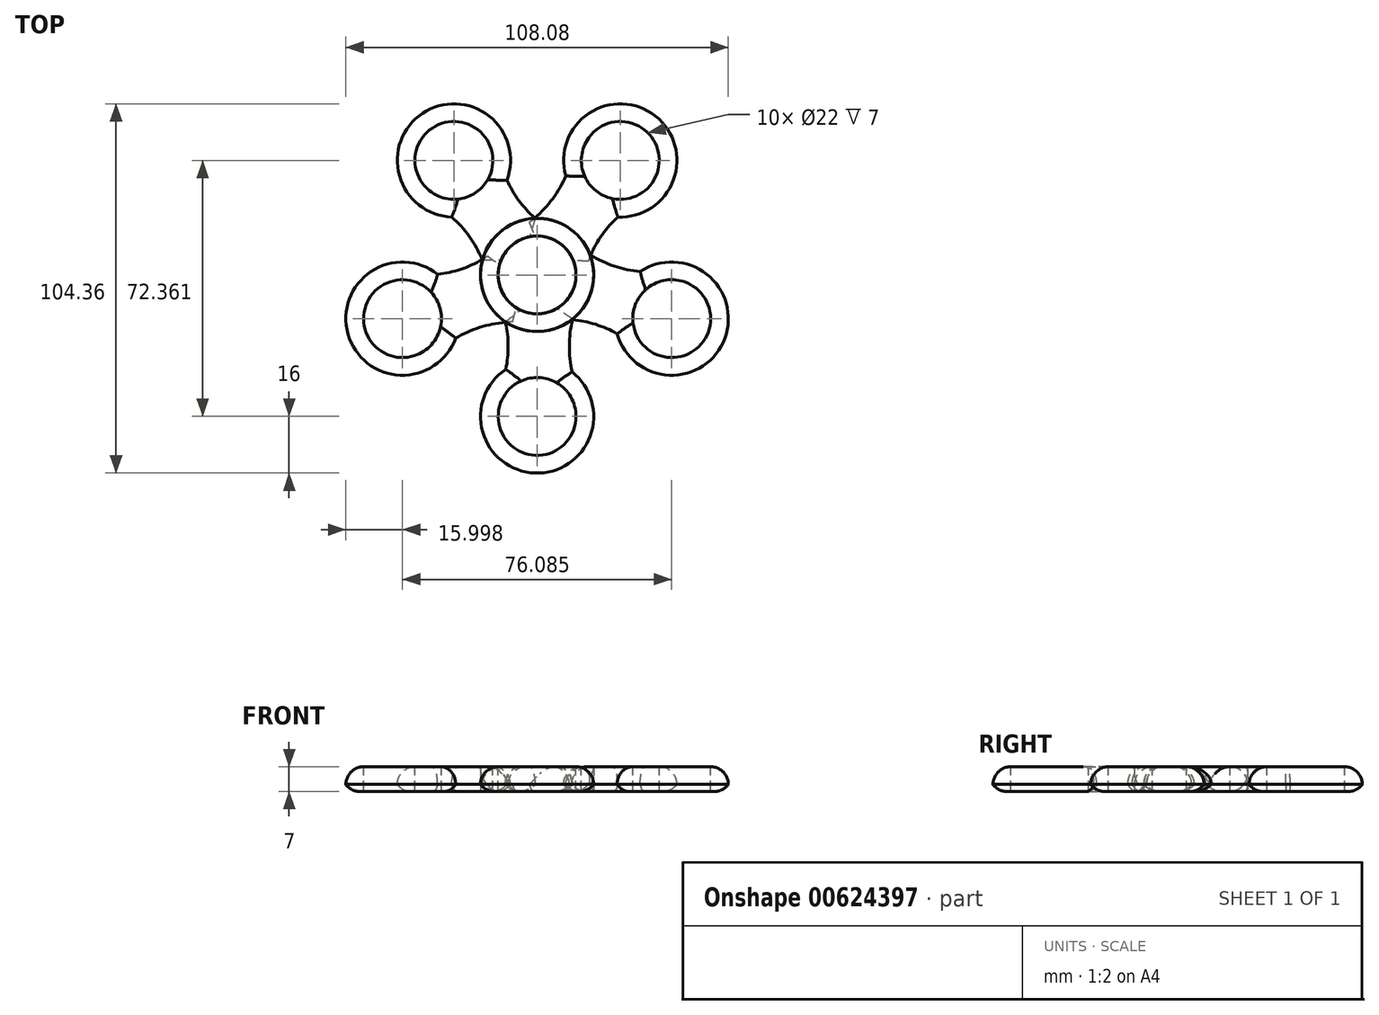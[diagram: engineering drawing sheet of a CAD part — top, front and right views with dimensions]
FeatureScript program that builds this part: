
annotation { "Feature Type Name" : "Feature", "Feature Type Description" : "" }
export const myFeature = defineFeature(function(context is Context, id is Id, definition is map)
    precondition{}
    {
        {
            var Q0;
            Q0=qCreatedBy(makeId("Top.planeOp"),FACE);
            var sketch = newSketch(context, id + "F0", { "sketchPlane" : qUnion([Q0])});
            skCircle(sketch, "E0", {"center": v(0, 0) * mm, "radius": 16 * mm});
            skCircle(sketch, "E1", {"center": v(0, -40) * mm, "radius": 16 * mm});
            skArc(sketch, "E2", {"start": v(-16, -40.55) * mm, "mid": v(-8.17, -20.27) * mm, "end": v(-16, 0) * mm});
            skArc(sketch, "E3", {"start": v(16, 0) * mm, "mid": v(9.11, -20.27) * mm, "end": v(16, -40.55) * mm});
            skSolve(sketch);
        }
        {
            var Q0;
            Q0 = qSketchRegion(id + "F0", true);
            extrude(context, id + "F1", {"entities" : qUnion([Q0]), "depth" : 7 * mm, "offsetDistance" : 25 * mm});
        }
        {
            var Q0;
            Q0=makeQuery(id+"F1.opExtrude","CAP_FACE",FACE,{"disambiguationData":[OSD([sQuery(id+"F0.wireOp",EDGE,"E0"),sQuery(id+"F0.wireOp",EDGE,"E1"),sQuery(id+"F0.wireOp",EDGE,"Ue3lBEtB-XySh-TUo9-pEQx-awfWVajxnvRm"),sQuery(id+"F0.wireOp",EDGE,"Egq79wn7-ryfj-ZDxT-aGIX-HA1hZmSv7uEE")])],"isStart":false});
            var sketch = newSketch(context, id + "F2", { "sketchPlane" : qUnion([Q0])});
            skCircle(sketch, "E4", {"center": v(0, 0) * mm, "radius": 11 * mm});
            skCircle(sketch, "E5", {"center": v(0, -40) * mm, "radius": 11 * mm});
            skSolve(sketch);
        }
        {
            var Q0;
            Q0 = qSketchRegion(id + "F2", true);
            extrude(context, id + "F3", {"entities" : qUnion([Q0]), "operationType" : NewBodyOperationType.REMOVE, "endBound" : BoundingType.THROUGH_ALL, "oppositeDirection" : true, "depth" : 25 * mm, "offsetDistance" : 25 * mm});
        }
        {
            var Q0;
            Q0=qCreatedBy(makeId("Front.planeOp"),FACE);
            var sketch = newSketch(context, id + "F4", { "sketchPlane" : qUnion([Q0])});
            skLineSegment(sketch, "E6", {"start": v(0, 0) * mm, "end": v(0, 23.09) * mm});
            skSolve(sketch);
        }
        {
            var Q0;
            Q0=makeQuery(id+"F1.opExtrude","SWEPT_BODY",BODY,{"disambiguationData":[OSD([sQuery(id+"F0.wireOp",EDGE,"E0"),sQuery(id+"F0.wireOp",EDGE,"E1"),sQuery(id+"F0.wireOp",EDGE,"Ue3lBEtB-XySh-TUo9-pEQx-awfWVajxnvRm"),sQuery(id+"F0.wireOp",EDGE,"Egq79wn7-ryfj-ZDxT-aGIX-HA1hZmSv7uEE")])]});
            var Q1;
            Q1=sQuery(id+"F4.wireOp",EDGE,"E6");
            circularPattern(context, id + "F5", {"entities" : qUnion([Q0]), "axis" : qUnion([Q1]), "angle" : 360 * degree, "instanceCount" : 5, "equalSpace" : true});
        }
        {
            var Q0;
            Q0=makeQuery(id+"F5.opPattern","COPY",EDGE,{"derivedFrom":makeQuery(id+"F1.opExtrude","CAP_EDGE",EDGE,{"disambiguationData":[OSD([sQuery(id+"F0.wireOp",EDGE,"E1")])],"isStart":false}),"instanceName":"4"});
            var Q1;
            Q1=makeQuery(id+"F5.opPattern","COPY",EDGE,{"derivedFrom":makeQuery(id+"F1.opExtrude","CAP_EDGE",EDGE,{"disambiguationData":[OSD([sQuery(id+"F0.wireOp",EDGE,"E3")])],"isStart":false}),"instanceName":"4"});
            var Q2;
            Q2=makeQuery(id+"F1.opExtrude","CAP_EDGE",EDGE,{"disambiguationData":[OSD([sQuery(id+"F0.wireOp",EDGE,"E2")])],"isStart":false});
            var Q3;
            Q3=makeQuery(id+"F1.opExtrude","CAP_EDGE",EDGE,{"disambiguationData":[OSD([sQuery(id+"F0.wireOp",EDGE,"E1")])],"isStart":false});
            var Q4;
            Q4=makeQuery(id+"F1.opExtrude","CAP_EDGE",EDGE,{"disambiguationData":[OSD([sQuery(id+"F0.wireOp",EDGE,"E3")])],"isStart":false});
            var Q5;
            Q5=makeQuery(id+"F5.opPattern","COPY",EDGE,{"derivedFrom":makeQuery(id+"F1.opExtrude","CAP_EDGE",EDGE,{"disambiguationData":[OSD([sQuery(id+"F0.wireOp",EDGE,"E2")])],"isStart":false}),"instanceName":"1"});
            var Q6;
            Q6=makeQuery(id+"F5.opPattern","COPY",EDGE,{"derivedFrom":makeQuery(id+"F1.opExtrude","CAP_EDGE",EDGE,{"disambiguationData":[OSD([sQuery(id+"F0.wireOp",EDGE,"E1")])],"isStart":false}),"instanceName":"1"});
            var Q7;
            Q7=makeQuery(id+"F5.opPattern","COPY",EDGE,{"derivedFrom":makeQuery(id+"F1.opExtrude","CAP_EDGE",EDGE,{"disambiguationData":[OSD([sQuery(id+"F0.wireOp",EDGE,"E3")])],"isStart":false}),"instanceName":"1"});
            var Q8;
            Q8=makeQuery(id+"F5.opPattern","COPY",EDGE,{"derivedFrom":makeQuery(id+"F1.opExtrude","CAP_EDGE",EDGE,{"disambiguationData":[OSD([sQuery(id+"F0.wireOp",EDGE,"E2")])],"isStart":false}),"instanceName":"2"});
            var Q9;
            Q9=makeQuery(id+"F5.opPattern","COPY",EDGE,{"derivedFrom":makeQuery(id+"F1.opExtrude","CAP_EDGE",EDGE,{"disambiguationData":[OSD([sQuery(id+"F0.wireOp",EDGE,"E1")])],"isStart":false}),"instanceName":"2"});
            var Q10;
            Q10=makeQuery(id+"F5.opPattern","COPY",EDGE,{"derivedFrom":makeQuery(id+"F1.opExtrude","CAP_EDGE",EDGE,{"disambiguationData":[OSD([sQuery(id+"F0.wireOp",EDGE,"E3")])],"isStart":false}),"instanceName":"2"});
            var Q11;
            Q11=makeQuery(id+"F5.opPattern","COPY",EDGE,{"derivedFrom":makeQuery(id+"F1.opExtrude","CAP_EDGE",EDGE,{"disambiguationData":[OSD([sQuery(id+"F0.wireOp",EDGE,"E2")])],"isStart":false}),"instanceName":"3"});
            var Q12;
            Q12=makeQuery(id+"F5.opPattern","COPY",EDGE,{"derivedFrom":makeQuery(id+"F1.opExtrude","CAP_EDGE",EDGE,{"disambiguationData":[OSD([sQuery(id+"F0.wireOp",EDGE,"E1")])],"isStart":false}),"instanceName":"3"});
            var Q13;
            Q13=makeQuery(id+"F5.opPattern","COPY",EDGE,{"derivedFrom":makeQuery(id+"F1.opExtrude","CAP_EDGE",EDGE,{"disambiguationData":[OSD([sQuery(id+"F0.wireOp",EDGE,"E3")])],"isStart":false}),"instanceName":"3"});
            var Q14;
            Q14=makeQuery(id+"F5.opPattern","COPY",EDGE,{"derivedFrom":makeQuery(id+"F1.opExtrude","CAP_EDGE",EDGE,{"disambiguationData":[OSD([sQuery(id+"F0.wireOp",EDGE,"E2")])],"isStart":false}),"instanceName":"4"});
            fillet(context, id + "F6", {"entities" : qUnion([Q0, Q1, Q2, Q3, Q4, Q5, Q6, Q7, Q8, Q9, Q10, Q11, Q12, Q13, Q14]), "radius" : 5 * mm, "tangentPropagation" : true, "allowEdgeOverflow" : false});
        }
        {
            var Q0;
            Q0=makeQuery(id+"F5.opPattern","COPY",EDGE,{"derivedFrom":makeQuery(id+"F1.opExtrude","CAP_EDGE",EDGE,{"disambiguationData":[OSD([sQuery(id+"F0.wireOp",EDGE,"E1")])],"isStart":true}),"instanceName":"4"});
            var Q1;
            Q1=makeQuery(id+"F5.opPattern","COPY",EDGE,{"derivedFrom":makeQuery(id+"F1.opExtrude","CAP_EDGE",EDGE,{"disambiguationData":[OSD([sQuery(id+"F0.wireOp",EDGE,"E3")])],"isStart":true}),"instanceName":"4"});
            var Q2;
            Q2=makeQuery(id+"F1.opExtrude","CAP_EDGE",EDGE,{"disambiguationData":[OSD([sQuery(id+"F0.wireOp",EDGE,"E2")])],"isStart":true});
            var Q3;
            Q3=makeQuery(id+"F1.opExtrude","CAP_EDGE",EDGE,{"disambiguationData":[OSD([sQuery(id+"F0.wireOp",EDGE,"E1")])],"isStart":true});
            var Q4;
            Q4=makeQuery(id+"F1.opExtrude","CAP_EDGE",EDGE,{"disambiguationData":[OSD([sQuery(id+"F0.wireOp",EDGE,"E3")])],"isStart":true});
            var Q5;
            Q5=makeQuery(id+"F5.opPattern","COPY",EDGE,{"derivedFrom":makeQuery(id+"F1.opExtrude","CAP_EDGE",EDGE,{"disambiguationData":[OSD([sQuery(id+"F0.wireOp",EDGE,"E2")])],"isStart":true}),"instanceName":"1"});
            var Q6;
            Q6=makeQuery(id+"F5.opPattern","COPY",EDGE,{"derivedFrom":makeQuery(id+"F1.opExtrude","CAP_EDGE",EDGE,{"disambiguationData":[OSD([sQuery(id+"F0.wireOp",EDGE,"E1")])],"isStart":true}),"instanceName":"1"});
            var Q7;
            Q7=makeQuery(id+"F5.opPattern","COPY",EDGE,{"derivedFrom":makeQuery(id+"F1.opExtrude","CAP_EDGE",EDGE,{"disambiguationData":[OSD([sQuery(id+"F0.wireOp",EDGE,"E3")])],"isStart":true}),"instanceName":"1"});
            var Q8;
            Q8=makeQuery(id+"F5.opPattern","COPY",EDGE,{"derivedFrom":makeQuery(id+"F1.opExtrude","CAP_EDGE",EDGE,{"disambiguationData":[OSD([sQuery(id+"F0.wireOp",EDGE,"E2")])],"isStart":true}),"instanceName":"2"});
            var Q9;
            Q9=makeQuery(id+"F5.opPattern","COPY",EDGE,{"derivedFrom":makeQuery(id+"F1.opExtrude","CAP_EDGE",EDGE,{"disambiguationData":[OSD([sQuery(id+"F0.wireOp",EDGE,"E1")])],"isStart":true}),"instanceName":"2"});
            var Q10;
            Q10=makeQuery(id+"F5.opPattern","COPY",EDGE,{"derivedFrom":makeQuery(id+"F1.opExtrude","CAP_EDGE",EDGE,{"disambiguationData":[OSD([sQuery(id+"F0.wireOp",EDGE,"E3")])],"isStart":true}),"instanceName":"2"});
            var Q11;
            Q11=makeQuery(id+"F5.opPattern","COPY",EDGE,{"derivedFrom":makeQuery(id+"F1.opExtrude","CAP_EDGE",EDGE,{"disambiguationData":[OSD([sQuery(id+"F0.wireOp",EDGE,"E2")])],"isStart":true}),"instanceName":"3"});
            var Q12;
            Q12=makeQuery(id+"F5.opPattern","COPY",EDGE,{"derivedFrom":makeQuery(id+"F1.opExtrude","CAP_EDGE",EDGE,{"disambiguationData":[OSD([sQuery(id+"F0.wireOp",EDGE,"E3")])],"isStart":true}),"instanceName":"3"});
            var Q13;
            Q13=makeQuery(id+"F5.opPattern","COPY",EDGE,{"derivedFrom":makeQuery(id+"F1.opExtrude","CAP_EDGE",EDGE,{"disambiguationData":[OSD([sQuery(id+"F0.wireOp",EDGE,"E1")])],"isStart":true}),"instanceName":"3"});
            var Q14;
            Q14=makeQuery(id+"F5.opPattern","COPY",EDGE,{"derivedFrom":makeQuery(id+"F1.opExtrude","CAP_EDGE",EDGE,{"disambiguationData":[OSD([sQuery(id+"F0.wireOp",EDGE,"E2")])],"isStart":true}),"instanceName":"4"});
            fillet(context, id + "F7", {"entities" : qUnion([Q0, Q1, Q2, Q3, Q4, Q5, Q6, Q7, Q8, Q9, Q10, Q11, Q12, Q13, Q14]), "radius" : 5 * mm, "tangentPropagation" : true, "allowEdgeOverflow" : false});
        }
        {
            var Q0;
            Q0=makeQuery(id+"F5.opPattern","COPY",EDGE,{"derivedFrom":makeQuery(id+"F1.opExtrude","CAP_EDGE",EDGE,{"disambiguationData":[OSD([sQuery(id+"F0.wireOp",EDGE,"E0")])],"isStart":true}),"instanceName":"2"});
            var Q1;
            Q1=makeQuery(id+"F5.opPattern","COPY",EDGE,{"derivedFrom":makeQuery(id+"F1.opExtrude","CAP_EDGE",EDGE,{"disambiguationData":[OSD([sQuery(id+"F0.wireOp",EDGE,"E0")])],"isStart":true}),"instanceName":"4"});
            fillet(context, id + "F8", {"entities" : qUnion([Q0, Q1]), "radius" : 5 * mm, "tangentPropagation" : true, "allowEdgeOverflow" : false});
        }
        {
            var Q0;
            Q0=makeQuery(id+"F1.opExtrude","CAP_EDGE",EDGE,{"disambiguationData":[OSD([sQuery(id+"F0.wireOp",EDGE,"E0")])],"isStart":false});
            var Q1;
            Q1=makeQuery(id+"F5.opPattern","COPY",EDGE,{"derivedFrom":makeQuery(id+"F1.opExtrude","CAP_EDGE",EDGE,{"disambiguationData":[OSD([sQuery(id+"F0.wireOp",EDGE,"E0")])],"isStart":false}),"instanceName":"3"});
            fillet(context, id + "F9", {"entities" : qUnion([Q0, Q1]), "radius" : 5 * mm, "tangentPropagation" : true, "allowEdgeOverflow" : false});
        }
    });
